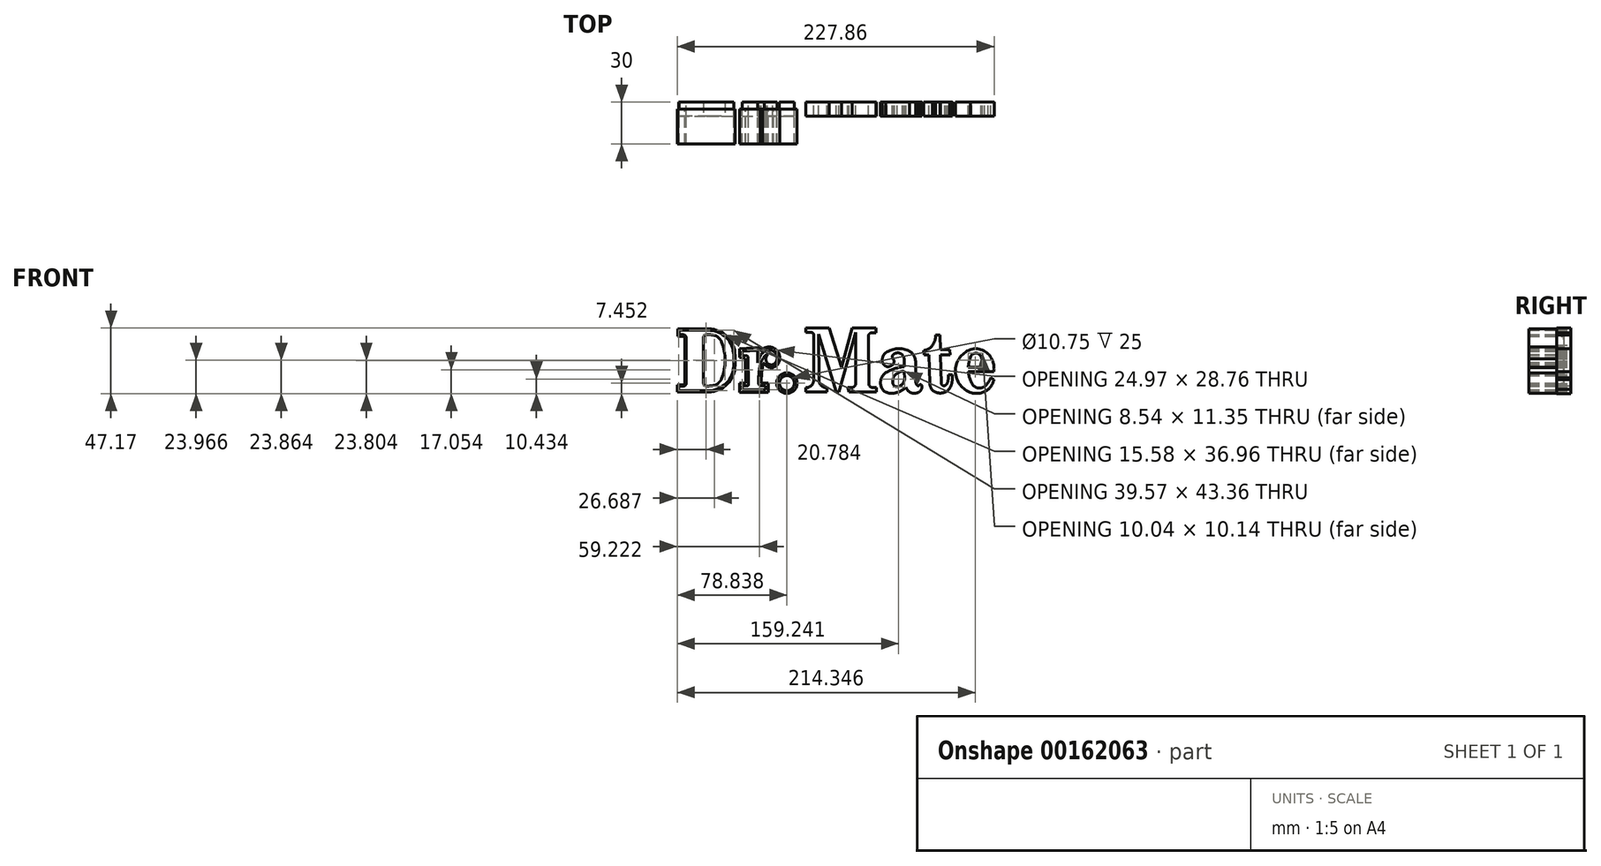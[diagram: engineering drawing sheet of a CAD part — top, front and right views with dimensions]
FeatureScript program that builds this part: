
annotation { "Feature Type Name" : "Feature", "Feature Type Description" : "" }
export const myFeature = defineFeature(function(context is Context, id is Id, definition is map)
    precondition{}
    {
        {
            var Q0;
            Q0=qCreatedBy(makeId("Front.planeOp"),FACE);
            var sketch = newSketch(context, id + "F0", { "sketchPlane" : qUnion([Q0])});
            skLineSegment(sketch, "E0", {"start": v(23.83, 45.48) * mm, "end": v(2.7, 45.48) * mm});
            skLineSegment(sketch, "E1", {"start": v(2.7, 45.48) * mm, "end": v(2.7, 42.24) * mm});
            skLineSegment(sketch, "E2", {"start": v(2.7, 42.24) * mm, "end": v(5.73, 42.24) * mm});
            skLineSegment(sketch, "E3", {"start": v(7.73, 40.24) * mm, "end": v(7.73, 7.24) * mm});
            skLineSegment(sketch, "E4", {"start": v(5.73, 5.24) * mm, "end": v(2.36, 5.24) * mm});
            skLineSegment(sketch, "E5", {"start": v(2.36, 5.24) * mm, "end": v(2.36, 2.11) * mm});
            skLineSegment(sketch, "E6", {"start": v(2.36, 2.11) * mm, "end": v(23.83, 2.11) * mm});
            skPoint(sketch, "E7.visualSharp", {"position": v(7.73, 42.24) * mm});
            skArc(sketch, "E7.filletArc", {"start": v(7.73, 40.24) * mm, "mid": v(7.14, 41.66) * mm, "end": v(5.73, 42.24) * mm});
            skPoint(sketch, "E8.visualSharp", {"position": v(7.73, 5.24) * mm});
            skArc(sketch, "E8.filletArc", {"start": v(5.73, 5.24) * mm, "mid": v(7.14, 5.83) * mm, "end": v(7.73, 7.24) * mm});
            skLineSegment(sketch, "E9", {"start": v(41.93, 27.38) * mm, "end": v(41.93, 20.21) * mm});
            skPoint(sketch, "E10.visualSharp", {"position": v(41.93, 45.48) * mm});
            skArc(sketch, "E10.filletArc", {"start": v(41.93, 27.38) * mm, "mid": v(36.63, 40.17) * mm, "end": v(23.83, 45.48) * mm});
            skPoint(sketch, "E11.visualSharp", {"position": v(41.93, 2.11) * mm});
            skArc(sketch, "E11.filletArc", {"start": v(23.83, 2.11) * mm, "mid": v(36.63, 7.41) * mm, "end": v(41.93, 20.21) * mm});
            skSolve(sketch);
        }
        {
            var Q0;
            Q0 = qSketchRegion(id + "F0", true);
            extrude(context, id + "F1", {"entities" : qUnion([Q0]), "endBound" : BoundingType.SYMMETRIC, "depth" : 10 * mm});
        }
        {
            var Q0;
            Q0=qCreatedBy(makeId("Front.planeOp"),FACE);
            var sketch = newSketch(context, id + "F2", { "sketchPlane" : qUnion([Q0])});
            skLineSegment(sketch, "E12", {"start": v(20.26, 40.33) * mm, "end": v(20.26, 7.37) * mm});
            skLineSegment(sketch, "E13", {"start": v(22.26, 5.37) * mm, "end": v(23.68, 5.37) * mm});
            skLineSegment(sketch, "E14", {"start": v(22.26, 42.33) * mm, "end": v(23.68, 42.33) * mm});
            skPoint(sketch, "E15.visualSharp", {"position": v(20.26, 42.33) * mm});
            skArc(sketch, "E15.filletArc", {"start": v(22.26, 42.33) * mm, "mid": v(20.84, 41.75) * mm, "end": v(20.26, 40.33) * mm});
            skPoint(sketch, "E16.visualSharp", {"position": v(20.26, 5.37) * mm});
            skArc(sketch, "E16.filletArc", {"start": v(20.26, 7.37) * mm, "mid": v(20.84, 5.96) * mm, "end": v(22.26, 5.37) * mm});
            skPoint(sketch, "E17.visualSharp", {"position": v(41.68, 42.33) * mm});
            skArc(sketch, "E17.filletArc", {"start": v(29.92, 41.22) * mm, "mid": v(26.85, 42.05) * mm, "end": v(23.68, 42.33) * mm});
            skPoint(sketch, "E18.visualSharp", {"position": v(41.68, 5.37) * mm});
            skArc(sketch, "E18.filletArc", {"start": v(23.68, 5.37) * mm, "mid": v(26.85, 5.66) * mm, "end": v(29.92, 6.49) * mm});
            skArc(sketch, "E19", {"start": v(29.92, 6.49) * mm, "mid": v(31.56, 8.17) * mm, "end": v(33.02, 10) * mm});
            skArc(sketch, "E20.trimOffspring", {"start": v(33.02, 37.7) * mm, "mid": v(31.56, 39.54) * mm, "end": v(29.92, 41.22) * mm});
            skArc(sketch, "E21", {"start": v(33.02, 10) * mm, "mid": v(35.84, 23.85) * mm, "end": v(33.02, 37.7) * mm});
            skSolve(sketch);
        }
        {
            var Q0;
            Q0 = qSketchRegion(id + "F2", true);
            extrude(context, id + "F3", {"entities" : qUnion([Q0]), "operationType" : NewBodyOperationType.REMOVE, "endBound" : BoundingType.SYMMETRIC, "oppositeDirection" : true, "depth" : 25 * mm});
        }
        {
            var Q0;
            Q0=makeQuery(id+"F3.boolean.opBoolean","COPY",EDGE,{"derivedFrom":makeQuery(id+"F3.opExtrude","SWEPT_EDGE",EDGE,{"disambiguationData":[OSD([sQuery(id+"F2.wireOp",EDGE,"E19"),sQuery(id+"F2.wireOp",EDGE,"E21")])]})});
            var Q1;
            Q1=makeQuery(id+"F3.boolean.opBoolean","COPY",EDGE,{"derivedFrom":makeQuery(id+"F3.opExtrude","SWEPT_EDGE",EDGE,{"disambiguationData":[OSD([sQuery(id+"F2.wireOp",EDGE,"E18.filletArc"),sQuery(id+"F2.wireOp",EDGE,"E19")])]})});
            var Q2;
            Q2=makeQuery(id+"F3.boolean.opBoolean","COPY",EDGE,{"derivedFrom":makeQuery(id+"F3.opExtrude","SWEPT_EDGE",EDGE,{"disambiguationData":[OSD([sQuery(id+"F2.wireOp",EDGE,"E20.trimOffspring"),sQuery(id+"F2.wireOp",EDGE,"E21")])]})});
            var Q3;
            Q3=makeQuery(id+"F3.boolean.opBoolean","COPY",EDGE,{"derivedFrom":makeQuery(id+"F3.opExtrude","SWEPT_EDGE",EDGE,{"disambiguationData":[OSD([sQuery(id+"F2.wireOp",EDGE,"E17.filletArc"),sQuery(id+"F2.wireOp",EDGE,"E20.trimOffspring")])]})});
            fillet(context, id + "F4", {"entities" : qUnion([Q0, Q1, Q2, Q3]), "radius" : 5 * mm, "tangentPropagation" : true, "allowEdgeOverflow" : false});
        }
        {
            var Q0;
            Q0=qCreatedBy(makeId("Front.planeOp"),FACE);
            var sketch = newSketch(context, id + "F5", { "sketchPlane" : qUnion([Q0])});
            skLineSegment(sketch, "E22", {"start": v(48.1, 30.42) * mm, "end": v(48.1, 27.61) * mm});
            skLineSegment(sketch, "E23", {"start": v(48.1, 30.42) * mm, "end": v(59.09, 30.93) * mm});
            skLineSegment(sketch, "E24", {"start": v(48.1, 2.66) * mm, "end": v(64.8, 2.66) * mm});
            skLineSegment(sketch, "E25", {"start": v(59.09, 30.93) * mm, "end": v(59.09, 22.2) * mm});
            skLineSegment(sketch, "E26", {"start": v(48.1, 5.47) * mm, "end": v(51.51, 5.47) * mm});
            skLineSegment(sketch, "E27", {"start": v(48.1, 27.61) * mm, "end": v(51.46, 27.04) * mm});
            skLineSegment(sketch, "E28", {"start": v(64.8, 5.47) * mm, "end": v(64.8, 2.66) * mm});
            skLineSegment(sketch, "E29.trimOffspring", {"start": v(52.29, 26.06) * mm, "end": v(52.51, 6.48) * mm});
            skLineSegment(sketch, "E30.trimOffspring", {"start": v(61.83, 5.47) * mm, "end": v(64.8, 5.47) * mm});
            skLineSegment(sketch, "E31.trimOffspring", {"start": v(48.1, 5.47) * mm, "end": v(48.1, 2.66) * mm});
            skArc(sketch, "E32", {"start": v(73.07, 24.94) * mm, "mid": v(70.3, 30.62) * mm, "end": v(64, 30.34) * mm});
            skArc(sketch, "E33", {"start": v(69.92, 20.7) * mm, "mid": v(72.14, 22.34) * mm, "end": v(73.07, 24.94) * mm});
            skArc(sketch, "E34", {"start": v(64, 30.34) * mm, "mid": v(60.9, 26.65) * mm, "end": v(59.09, 22.2) * mm});
            skArc(sketch, "E35", {"start": v(65.86, 22.25) * mm, "mid": v(67.65, 20.85) * mm, "end": v(69.92, 20.7) * mm});
            skArc(sketch, "E36", {"start": v(66.1, 27.52) * mm, "mid": v(65.06, 24.93) * mm, "end": v(65.86, 22.25) * mm});
            skArc(sketch, "E37", {"start": v(59.89, 6.98) * mm, "mid": v(60.62, 5.92) * mm, "end": v(61.83, 5.47) * mm});
            skArc(sketch, "E38", {"start": v(60.03, 13.08) * mm, "mid": v(59.8, 10.03) * mm, "end": v(59.89, 6.98) * mm});
            skArc(sketch, "E39", {"start": v(60.96, 20.37) * mm, "mid": v(60.34, 16.75) * mm, "end": v(60.03, 13.08) * mm});
            skArc(sketch, "E40", {"start": v(65.5, 27.94) * mm, "mid": v(62.63, 24.52) * mm, "end": v(60.96, 20.37) * mm});
            skArc(sketch, "E41", {"start": v(66.1, 27.52) * mm, "mid": v(65.98, 27.98) * mm, "end": v(65.5, 27.94) * mm});
            skPoint(sketch, "E42.visualSharp", {"position": v(52.28, 26.9) * mm});
            skArc(sketch, "E42.filletArc", {"start": v(52.29, 26.06) * mm, "mid": v(52.05, 26.7) * mm, "end": v(51.46, 27.04) * mm});
            skPoint(sketch, "E43.visualSharp", {"position": v(52.52, 5.47) * mm});
            skArc(sketch, "E43.filletArc", {"start": v(51.51, 5.47) * mm, "mid": v(52.22, 5.77) * mm, "end": v(52.51, 6.48) * mm});
            skSolve(sketch);
        }
        {
            var Q0;
            Q0 = qSketchRegion(id + "F5", true);
            extrude(context, id + "F6", {"entities" : qUnion([Q0]), "endBound" : BoundingType.SYMMETRIC, "depth" : 10 * mm});
        }
        {
            var Q0;
            Q0=qCreatedBy(makeId("Front.planeOp"),FACE);
            var sketch = newSketch(context, id + "F7", { "sketchPlane" : qUnion([Q0])});
            skCircle(sketch, "E44", {"center": v(80.2, 7.44) * mm, "radius": 5.38 * mm});
            skSolve(sketch);
        }
        {
            var Q0;
            Q0 = qSketchRegion(id + "F7", true);
            extrude(context, id + "F8", {"entities" : qUnion([Q0]), "endBound" : BoundingType.SYMMETRIC, "depth" : 10 * mm});
        }
        {
            var Q0;
            Q0=qCreatedBy(makeId("Front.planeOp"),FACE);
            var sketch = newSketch(context, id + "F9", { "sketchPlane" : qUnion([Q0])});
            skLineSegment(sketch, "E45", {"start": v(93.8, 47.16) * mm, "end": v(110.75, 47.16) * mm});
            skLineSegment(sketch, "E46", {"start": v(127.22, 47.16) * mm, "end": v(119.38, 19.02) * mm});
            skLineSegment(sketch, "E47", {"start": v(93.8, 47.16) * mm, "end": v(93.8, 43.88) * mm});
            skLineSegment(sketch, "E48", {"start": v(99.4, 42.37) * mm, "end": v(99.4, 9.27) * mm});
            skLineSegment(sketch, "E49", {"start": v(93.8, 1.02) * mm, "end": v(108.94, 1.02) * mm});
            skLineSegment(sketch, "E50", {"start": v(102.92, 42.74) * mm, "end": v(103.28, 9.22) * mm});
            skLineSegment(sketch, "E51", {"start": v(102.92, 42.74) * mm, "end": v(115.57, 1.02) * mm});
            skLineSegment(sketch, "E52", {"start": v(110.75, 47.16) * mm, "end": v(119.38, 19.02) * mm});
            skLineSegment(sketch, "E53", {"start": v(129.69, 43.89) * mm, "end": v(129.69, 7.07) * mm});
            skLineSegment(sketch, "E54", {"start": v(138.75, 40.98) * mm, "end": v(139.12, 7.04) * mm});
            skLineSegment(sketch, "E55", {"start": v(144.36, 47.16) * mm, "end": v(144.39, 43.8) * mm});
            skLineSegment(sketch, "E56", {"start": v(93.8, 43.88) * mm, "end": v(97.9, 43.87) * mm});
            skLineSegment(sketch, "E57.0", {"start": v(93.8, 4.27) * mm, "end": v(94.4, 4.27) * mm});
            skPoint(sketch, "E58.orphan", {"position": v(90.95, 43.89) * mm});
            skPoint(sketch, "E59.orphan", {"position": v(90.95, 47.16) * mm});
            skLineSegment(sketch, "E60.trimOffspring", {"start": v(144.68, 4.27) * mm, "end": v(144.7, 1.02) * mm});
            skLineSegment(sketch, "E61.trimOffspring", {"start": v(141.56, 43.8) * mm, "end": v(144.39, 43.8) * mm});
            skLineSegment(sketch, "E62.trimOffspring", {"start": v(127.22, 47.16) * mm, "end": v(144.36, 47.16) * mm});
            skLineSegment(sketch, "E63.trimOffspring", {"start": v(93.8, 4.27) * mm, "end": v(93.8, 1.02) * mm});
            skLineSegment(sketch, "E64.trimOffspring", {"start": v(117.74, 1.02) * mm, "end": v(129.69, 43.89) * mm});
            skLineSegment(sketch, "E65.trimOffspring", {"start": v(123.9, 4.27) * mm, "end": v(124.9, 1.02) * mm});
            skLineSegment(sketch, "E66.trimOffspring", {"start": v(108.28, 4.27) * mm, "end": v(108.96, 4.27) * mm});
            skLineSegment(sketch, "E67.trimOffspring", {"start": v(123.9, 4.27) * mm, "end": v(126.89, 4.27) * mm});
            skLineSegment(sketch, "E68.trimOffspring", {"start": v(124.9, 1.02) * mm, "end": v(144.7, 1.02) * mm});
            skLineSegment(sketch, "E69.trimOffspring", {"start": v(141.92, 4.27) * mm, "end": v(144.68, 4.27) * mm});
            skPoint(sketch, "E70.startSnap0", {"position": v(108.96, 4.27) * mm});
            skLineSegment(sketch, "E71", {"start": v(108.94, 4.27) * mm, "end": v(108.94, 1.02) * mm});
            skLineSegment(sketch, "E72.trimOffspring", {"start": v(115.57, 1.02) * mm, "end": v(117.74, 1.02) * mm});
            skPoint(sketch, "E73.visualSharp", {"position": v(99.4, 43.87) * mm});
            skArc(sketch, "E73.filletArc", {"start": v(99.4, 42.37) * mm, "mid": v(98.96, 43.43) * mm, "end": v(97.9, 43.87) * mm});
            skPoint(sketch, "E74.visualSharp", {"position": v(99.4, 4.27) * mm});
            skArc(sketch, "E74.filletArc", {"start": v(94.4, 4.27) * mm, "mid": v(97.94, 5.74) * mm, "end": v(99.4, 9.27) * mm});
            skPoint(sketch, "E75.visualSharp", {"position": v(103.34, 4.27) * mm});
            skArc(sketch, "E75.filletArc", {"start": v(103.28, 9.22) * mm, "mid": v(104.77, 5.72) * mm, "end": v(108.28, 4.27) * mm});
            skPoint(sketch, "E76.visualSharp", {"position": v(129.69, 4.27) * mm});
            skArc(sketch, "E76.filletArc", {"start": v(126.89, 4.27) * mm, "mid": v(128.87, 5.1) * mm, "end": v(129.69, 7.07) * mm});
            skPoint(sketch, "E77.visualSharp", {"position": v(139.15, 4.27) * mm});
            skArc(sketch, "E77.filletArc", {"start": v(139.12, 7.04) * mm, "mid": v(139.95, 5.08) * mm, "end": v(141.92, 4.27) * mm});
            skPoint(sketch, "E78.visualSharp", {"position": v(138.72, 43.81) * mm});
            skArc(sketch, "E78.filletArc", {"start": v(141.56, 43.8) * mm, "mid": v(139.56, 42.98) * mm, "end": v(138.75, 40.98) * mm});
            skSolve(sketch);
        }
        {
            var Q0;
            Q0 = qSketchRegion(id + "F9", true);
            extrude(context, id + "F10", {"entities" : qUnion([Q0]), "endBound" : BoundingType.SYMMETRIC, "depth" : 10 * mm});
        }
        {
            var Q0;
            Q0=qCreatedBy(makeId("Front.planeOp"),FACE);
            var sketch = newSketch(context, id + "F11", { "sketchPlane" : qUnion([Q0])});
            skArc(sketch, "E79", {"start": v(172.7, 22.65) * mm, "mid": v(171.66, 27.12) * mm, "end": v(168.48, 30.43) * mm});
            skLineSegment(sketch, "E80", {"start": v(172.7, 22.65) * mm, "end": v(172.93, 8.42) * mm});
            skArc(sketch, "E81", {"start": v(168.48, 30.43) * mm, "mid": v(159.76, 32.2) * mm, "end": v(151.36, 29.26) * mm});
            skArc(sketch, "E82", {"start": v(151.36, 29.26) * mm, "mid": v(149.3, 26.59) * mm, "end": v(148.75, 23.26) * mm});
            skArc(sketch, "E83", {"start": v(148.75, 23.26) * mm, "mid": v(149.95, 20.7) * mm, "end": v(152.36, 19.26) * mm});
            skArc(sketch, "E84", {"start": v(152.36, 19.26) * mm, "mid": v(155.23, 19.9) * mm, "end": v(157.14, 22.15) * mm});
            skArc(sketch, "E85", {"start": v(157.14, 22.15) * mm, "mid": v(157.07, 24.2) * mm, "end": v(155.97, 25.93) * mm});
            skArc(sketch, "E86", {"start": v(156.97, 28.2) * mm, "mid": v(156.13, 27.22) * mm, "end": v(155.97, 25.93) * mm});
            skArc(sketch, "E87", {"start": v(164.45, 25.33) * mm, "mid": v(161.55, 28.93) * mm, "end": v(156.97, 28.2) * mm});
            skLineSegment(sketch, "E88", {"start": v(164.45, 25.33) * mm, "end": v(164.87, 11.05) * mm});
            skArc(sketch, "E89", {"start": v(164.74, 15.46) * mm, "mid": v(164.18, 15.94) * mm, "end": v(163.46, 16.1) * mm});
            skArc(sketch, "E90", {"start": v(164.63, 19.28) * mm, "mid": v(157.74, 17.88) * mm, "end": v(151.36, 14.93) * mm});
            skArc(sketch, "E91", {"start": v(151.36, 14.93) * mm, "mid": v(147.6, 8.68) * mm, "end": v(150.1, 1.82) * mm});
            skArc(sketch, "E92", {"start": v(150.1, 1.82) * mm, "mid": v(153.65, 0.29) * mm, "end": v(157.51, 0.28) * mm});
            skArc(sketch, "E93", {"start": v(157.51, 0.28) * mm, "mid": v(162.02, 1.68) * mm, "end": v(165.85, 4.44) * mm});
            skArc(sketch, "E94", {"start": v(159.52, 4.75) * mm, "mid": v(163.4, 6.87) * mm, "end": v(164.87, 11.05) * mm});
            skArc(sketch, "E95", {"start": v(156.5, 7.23) * mm, "mid": v(157.54, 5.41) * mm, "end": v(159.52, 4.75) * mm});
            skArc(sketch, "E96", {"start": v(157.54, 12.92) * mm, "mid": v(156.46, 10.18) * mm, "end": v(156.5, 7.23) * mm});
            skPoint(sketch, "E96.startSnap0", {"position": v(157.54, 5.41) * mm});
            skArc(sketch, "E97", {"start": v(163.46, 16.1) * mm, "mid": v(160.31, 14.86) * mm, "end": v(157.54, 12.92) * mm});
            skArc(sketch, "E98", {"start": v(172.93, 8.42) * mm, "mid": v(173.22, 7) * mm, "end": v(174.02, 5.8) * mm});
            skArc(sketch, "E99", {"start": v(174.02, 5.8) * mm, "mid": v(174.98, 5.66) * mm, "end": v(175.7, 6.3) * mm});
            skArc(sketch, "E100", {"start": v(177.42, 5.6) * mm, "mid": v(176.71, 6.32) * mm, "end": v(175.7, 6.3) * mm});
            skArc(sketch, "E101", {"start": v(174.62, 0.74) * mm, "mid": v(176.77, 2.73) * mm, "end": v(177.42, 5.6) * mm});
            skArc(sketch, "E102", {"start": v(165.85, 4.44) * mm, "mid": v(167.1, 2.35) * mm, "end": v(168.94, 0.77) * mm});
            skArc(sketch, "E103", {"start": v(168.94, 0.77) * mm, "mid": v(171.78, 0.05) * mm, "end": v(174.62, 0.74) * mm});
            skSolve(sketch);
        }
        {
            var Q0;
            Q0 = qSketchRegion(id + "F11", true);
            extrude(context, id + "F12", {"entities" : qUnion([Q0]), "endBound" : BoundingType.SYMMETRIC, "depth" : 10 * mm});
        }
        {
            var Q0;
            Q0=qCreatedBy(makeId("Front.planeOp"),FACE);
            var sketch = newSketch(context, id + "F13", { "sketchPlane" : qUnion([Q0])});
            skLineSegment(sketch, "E104", {"start": v(187.18, 42.16) * mm, "end": v(190.44, 42.1) * mm});
            skLineSegment(sketch, "E105", {"start": v(190.44, 42.1) * mm, "end": v(190.67, 31.73) * mm});
            skLineSegment(sketch, "E106", {"start": v(178.8, 27.63) * mm, "end": v(182.53, 27.63) * mm});
            skLineSegment(sketch, "E107", {"start": v(197.44, 31.73) * mm, "end": v(190.67, 31.73) * mm});
            skLineSegment(sketch, "E108", {"start": v(178.7, 31.04) * mm, "end": v(178.8, 27.63) * mm});
            skLineSegment(sketch, "E109", {"start": v(197.44, 31.73) * mm, "end": v(197.59, 27.63) * mm});
            skLineSegment(sketch, "E110", {"start": v(196.3, 13.37) * mm, "end": v(199.27, 13.37) * mm});
            skArc(sketch, "E111", {"start": v(182.9, 7.56) * mm, "mid": v(183.7, 4.23) * mm, "end": v(185.78, 1.52) * mm});
            skArc(sketch, "E112", {"start": v(185.78, 1.52) * mm, "mid": v(189.97, 0.3) * mm, "end": v(194.28, 0.99) * mm});
            skArc(sketch, "E113", {"start": v(194.28, 0.99) * mm, "mid": v(196.72, 3.04) * mm, "end": v(198.37, 5.77) * mm});
            skArc(sketch, "E114", {"start": v(198.37, 5.77) * mm, "mid": v(199.19, 9.53) * mm, "end": v(199.27, 13.37) * mm});
            skArc(sketch, "E115", {"start": v(191.2, 7.87) * mm, "mid": v(191.86, 6.09) * mm, "end": v(193.7, 5.6) * mm});
            skArc(sketch, "E116", {"start": v(193.7, 5.6) * mm, "mid": v(194.65, 6.17) * mm, "end": v(195.36, 7.01) * mm});
            skArc(sketch, "E117", {"start": v(195.36, 7.01) * mm, "mid": v(196.26, 10.12) * mm, "end": v(196.3, 13.37) * mm});
            skLineSegment(sketch, "E118.trimOffspring", {"start": v(190.76, 27.63) * mm, "end": v(197.59, 27.63) * mm});
            skLineSegment(sketch, "E119.trimOffspring", {"start": v(182.53, 27.63) * mm, "end": v(182.9, 7.56) * mm});
            skLineSegment(sketch, "E120.trimOffspring", {"start": v(190.76, 27.63) * mm, "end": v(191.22, 7.26) * mm});
            skPoint(sketch, "E121.visualSharp", {"position": v(182.26, 42.25) * mm});
            skArc(sketch, "E122", {"start": v(178.7, 31.04) * mm, "mid": v(182.27, 32.15) * mm, "end": v(185, 34.71) * mm});
            skArc(sketch, "E123", {"start": v(185, 34.71) * mm, "mid": v(186.7, 38.26) * mm, "end": v(187.18, 42.16) * mm});
            skSolve(sketch);
        }
        {
            var Q0;
            Q0 = qSketchRegion(id + "F13", true);
            extrude(context, id + "F14", {"entities" : qUnion([Q0]), "endBound" : BoundingType.SYMMETRIC, "depth" : 10 * mm});
        }
        {
            var Q0;
            Q0=qCreatedBy(makeId("Front.planeOp"),FACE);
            var sketch = newSketch(context, id + "F15", { "sketchPlane" : qUnion([Q0])});
            skLineSegment(sketch, "E124", {"start": v(210.69, 18.89) * mm, "end": v(220.1, 18.89) * mm});
            skLineSegment(sketch, "E125", {"start": v(210.74, 15.7) * mm, "end": v(229.12, 15.7) * mm});
            skLineSegment(sketch, "E126", {"start": v(226.7, 11.4) * mm, "end": v(229.2, 10.1) * mm});
            skArc(sketch, "E127", {"start": v(212.17, 31.58) * mm, "mid": v(201.46, 15.7) * mm, "end": v(213.05, 0.47) * mm});
            skArc(sketch, "E128", {"start": v(228.31, 23.2) * mm, "mid": v(221.93, 30.65) * mm, "end": v(212.17, 31.58) * mm});
            skArc(sketch, "E129.trimOffspring", {"start": v(229.12, 15.7) * mm, "mid": v(229.12, 19.5) * mm, "end": v(228.31, 23.2) * mm});
            skArc(sketch, "E130", {"start": v(219.75, 26.59) * mm, "mid": v(216.18, 29.03) * mm, "end": v(212.55, 26.67) * mm});
            skArc(sketch, "E131", {"start": v(220.58, 20.03) * mm, "mid": v(220.63, 23.37) * mm, "end": v(219.75, 26.59) * mm});
            skArc(sketch, "E132", {"start": v(220.1, 18.89) * mm, "mid": v(220.37, 19.45) * mm, "end": v(220.58, 20.03) * mm});
            skArc(sketch, "E133", {"start": v(213.05, 0.47) * mm, "mid": v(219.37, 0.28) * mm, "end": v(225.06, 3.02) * mm});
            skArc(sketch, "E134", {"start": v(225.06, 3.02) * mm, "mid": v(227.65, 6.26) * mm, "end": v(229.2, 10.1) * mm});
            skArc(sketch, "E135", {"start": v(213.34, 7.06) * mm, "mid": v(217.36, 4.02) * mm, "end": v(222.3, 5.01) * mm});
            skArc(sketch, "E136", {"start": v(222.3, 5.01) * mm, "mid": v(225.03, 7.85) * mm, "end": v(226.7, 11.4) * mm});
            skArc(sketch, "E137", {"start": v(212.55, 26.67) * mm, "mid": v(211.27, 22.86) * mm, "end": v(210.69, 18.89) * mm});
            skArc(sketch, "E138.trimOffspring", {"start": v(210.74, 15.7) * mm, "mid": v(211.6, 11.25) * mm, "end": v(213.34, 7.06) * mm});
            skSolve(sketch);
        }
        {
            var Q0;
            Q0 = qSketchRegion(id + "F15", true);
            extrude(context, id + "F16", {"entities" : qUnion([Q0]), "endBound" : BoundingType.SYMMETRIC, "depth" : 10 * mm});
        }
        {
            var Q0;
            Q0=qCreatedBy(makeId("Front.planeOp"),FACE);
            var sketch = newSketch(context, id + "F17", { "sketchPlane" : qUnion([Q0])});
            skLineSegment(sketch, "E139.0", {"start": v(22.26, 42.33) * mm, "end": v(23.68, 42.33) * mm});
            skArc(sketch, "E139.1", {"start": v(28.62, 41.64) * mm, "mid": v(29.82, 41.12) * mm, "end": v(30.85, 40.3) * mm});
            skArc(sketch, "E139.2", {"start": v(30.85, 7.4) * mm, "mid": v(29.82, 6.59) * mm, "end": v(28.62, 6.07) * mm});
            skArc(sketch, "E139.3", {"start": v(5.73, 5.24) * mm, "mid": v(7.14, 5.83) * mm, "end": v(7.73, 7.24) * mm});
            skArc(sketch, "E139.4", {"start": v(41.93, 27.38) * mm, "mid": v(36.63, 40.17) * mm, "end": v(23.83, 45.48) * mm});
            skArc(sketch, "E139.5", {"start": v(23.83, 2.11) * mm, "mid": v(36.63, 7.41) * mm, "end": v(41.93, 20.21) * mm});
            skArc(sketch, "E139.6", {"start": v(22.26, 42.33) * mm, "mid": v(20.84, 41.75) * mm, "end": v(20.26, 40.33) * mm});
            skArc(sketch, "E139.7", {"start": v(28.62, 41.64) * mm, "mid": v(26.18, 42.16) * mm, "end": v(23.68, 42.33) * mm});
            skArc(sketch, "E139.8", {"start": v(30.85, 7.4) * mm, "mid": v(31.76, 8.4) * mm, "end": v(32.6, 9.45) * mm});
            skArc(sketch, "E139.9", {"start": v(32.6, 38.26) * mm, "mid": v(31.76, 39.3) * mm, "end": v(30.85, 40.3) * mm});
            skArc(sketch, "E139.10", {"start": v(33.28, 10.63) * mm, "mid": v(35.84, 23.85) * mm, "end": v(33.28, 37.08) * mm});
            skArc(sketch, "E139.11", {"start": v(23.68, 5.37) * mm, "mid": v(26.18, 5.55) * mm, "end": v(28.62, 6.07) * mm});
            skLineSegment(sketch, "E139.12", {"start": v(23.83, 45.48) * mm, "end": v(2.7, 45.48) * mm});
            skLineSegment(sketch, "E139.13", {"start": v(2.7, 45.48) * mm, "end": v(2.7, 42.24) * mm});
            skLineSegment(sketch, "E139.16", {"start": v(22.26, 5.37) * mm, "end": v(23.68, 5.37) * mm});
            skLineSegment(sketch, "E139.20", {"start": v(20.26, 40.33) * mm, "end": v(20.26, 7.37) * mm});
            skArc(sketch, "E139.22", {"start": v(32.6, 38.26) * mm, "mid": v(32.98, 37.7) * mm, "end": v(33.28, 37.08) * mm});
            skArc(sketch, "E139.25", {"start": v(30.85, 40.3) * mm, "mid": v(29.82, 41.12) * mm, "end": v(28.62, 41.64) * mm});
            skArc(sketch, "E139.28", {"start": v(33.28, 10.63) * mm, "mid": v(32.98, 10.01) * mm, "end": v(32.6, 9.45) * mm});
            skLineSegment(sketch, "E139.29", {"start": v(41.93, 27.38) * mm, "end": v(41.93, 20.21) * mm});
            skArc(sketch, "E139.30", {"start": v(41.93, 27.38) * mm, "mid": v(36.63, 40.17) * mm, "end": v(23.83, 45.48) * mm});
            skLineSegment(sketch, "E139.31", {"start": v(2.7, 42.24) * mm, "end": v(5.73, 42.24) * mm});
            skArc(sketch, "E139.32", {"start": v(23.83, 2.11) * mm, "mid": v(36.63, 7.41) * mm, "end": v(41.93, 20.21) * mm});
            skLineSegment(sketch, "E139.33", {"start": v(7.73, 40.24) * mm, "end": v(7.73, 7.24) * mm});
            skLineSegment(sketch, "E139.34", {"start": v(5.73, 5.24) * mm, "end": v(2.36, 5.24) * mm});
            skLineSegment(sketch, "E139.35", {"start": v(2.36, 5.24) * mm, "end": v(2.36, 2.11) * mm});
            skLineSegment(sketch, "E139.36", {"start": v(2.36, 2.11) * mm, "end": v(23.83, 2.11) * mm});
            skArc(sketch, "E139.37", {"start": v(7.73, 40.24) * mm, "mid": v(7.14, 41.66) * mm, "end": v(5.73, 42.24) * mm});
            skArc(sketch, "E139.38", {"start": v(22.26, 42.33) * mm, "mid": v(20.84, 41.75) * mm, "end": v(20.26, 40.33) * mm});
            skArc(sketch, "E139.39", {"start": v(20.26, 7.37) * mm, "mid": v(20.84, 5.96) * mm, "end": v(22.26, 5.37) * mm});
            skArc(sketch, "E139.40", {"start": v(32.6, 38.26) * mm, "mid": v(31.76, 39.3) * mm, "end": v(30.85, 40.3) * mm});
            skArc(sketch, "E139.41", {"start": v(33.28, 10.63) * mm, "mid": v(35.84, 23.85) * mm, "end": v(33.28, 37.08) * mm});
            skLineSegment(sketch, "E139.42", {"start": v(2.7, 45.48) * mm, "end": v(2.7, 42.24) * mm});
            skLineSegment(sketch, "E139.53", {"start": v(23.83, 45.48) * mm, "end": v(2.7, 45.48) * mm});
            skLineSegment(sketch, "E139.54", {"start": v(22.26, 42.33) * mm, "end": v(23.68, 42.33) * mm});
            skLineSegment(sketch, "E139.58", {"start": v(20.26, 40.33) * mm, "end": v(20.26, 7.37) * mm});
            skLineSegment(sketch, "E139.59", {"start": v(22.26, 5.37) * mm, "end": v(23.68, 5.37) * mm});
            skArc(sketch, "E139.60", {"start": v(28.62, 6.07) * mm, "mid": v(29.82, 6.59) * mm, "end": v(30.85, 7.4) * mm});
            skLineSegment(sketch, "E139.64", {"start": v(41.93, 27.38) * mm, "end": v(41.93, 20.21) * mm});
            skLineSegment(sketch, "E139.65", {"start": v(2.7, 42.24) * mm, "end": v(5.73, 42.24) * mm});
            skLineSegment(sketch, "E139.66", {"start": v(7.73, 40.24) * mm, "end": v(7.73, 7.24) * mm});
            skLineSegment(sketch, "E139.67", {"start": v(5.73, 5.24) * mm, "end": v(2.36, 5.24) * mm});
            skLineSegment(sketch, "E139.68", {"start": v(2.36, 5.24) * mm, "end": v(2.36, 2.11) * mm});
            skLineSegment(sketch, "E139.69", {"start": v(2.36, 2.11) * mm, "end": v(23.83, 2.11) * mm});
            skArc(sketch, "E139.70", {"start": v(5.73, 5.24) * mm, "mid": v(7.14, 5.83) * mm, "end": v(7.73, 7.24) * mm});
            skArc(sketch, "E139.71", {"start": v(20.26, 7.37) * mm, "mid": v(20.84, 5.96) * mm, "end": v(22.26, 5.37) * mm});
            skArc(sketch, "E139.72", {"start": v(28.62, 41.64) * mm, "mid": v(26.18, 42.16) * mm, "end": v(23.68, 42.33) * mm});
            skArc(sketch, "E139.73", {"start": v(30.85, 7.4) * mm, "mid": v(31.76, 8.4) * mm, "end": v(32.6, 9.45) * mm});
            skArc(sketch, "E139.74", {"start": v(23.68, 5.37) * mm, "mid": v(26.18, 5.55) * mm, "end": v(28.62, 6.07) * mm});
            skArc(sketch, "E139.75", {"start": v(33.28, 37.08) * mm, "mid": v(32.98, 37.7) * mm, "end": v(32.6, 38.26) * mm});
            skArc(sketch, "E139.76", {"start": v(32.6, 9.45) * mm, "mid": v(32.98, 10.01) * mm, "end": v(33.28, 10.63) * mm});
            skArc(sketch, "E139.77", {"start": v(7.73, 40.24) * mm, "mid": v(7.14, 41.66) * mm, "end": v(5.73, 42.24) * mm});
            skLineSegment(sketch, "E140.0", {"start": v(22.26, 40.33) * mm, "end": v(22.26, 7.37) * mm});
            skLineSegment(sketch, "E141.0", {"start": v(22.26, 7.37) * mm, "end": v(23.68, 7.37) * mm});
            skArc(sketch, "E141.1", {"start": v(23.68, 7.37) * mm, "mid": v(26.3, 7.6) * mm, "end": v(28.85, 8.23) * mm});
            skArc(sketch, "E141.2", {"start": v(28.85, 8.23) * mm, "mid": v(30.12, 9.56) * mm, "end": v(31.27, 11) * mm});
            skLineSegment(sketch, "E141.3", {"start": v(22.26, 40.33) * mm, "end": v(23.68, 40.33) * mm});
            skArc(sketch, "E141.4", {"start": v(28.85, 39.47) * mm, "mid": v(26.3, 40.12) * mm, "end": v(23.68, 40.33) * mm});
            skArc(sketch, "E141.5", {"start": v(31.27, 36.71) * mm, "mid": v(30.12, 38.14) * mm, "end": v(28.85, 39.47) * mm});
            skArc(sketch, "E141.6", {"start": v(31.27, 11) * mm, "mid": v(33.84, 23.85) * mm, "end": v(31.27, 36.71) * mm});
            skLineSegment(sketch, "E142.0", {"start": v(23.83, 46.48) * mm, "end": v(1.7, 46.48) * mm});
            skArc(sketch, "E142.1", {"start": v(42.93, 27.38) * mm, "mid": v(37.33, 40.88) * mm, "end": v(23.83, 46.48) * mm});
            skLineSegment(sketch, "E142.2", {"start": v(1.7, 46.48) * mm, "end": v(1.7, 41.24) * mm});
            skLineSegment(sketch, "E142.3", {"start": v(42.93, 27.38) * mm, "end": v(42.93, 20.21) * mm});
            skArc(sketch, "E142.4", {"start": v(23.83, 1.11) * mm, "mid": v(37.33, 6.7) * mm, "end": v(42.93, 20.21) * mm});
            skLineSegment(sketch, "E142.5", {"start": v(1.36, 1.11) * mm, "end": v(23.83, 1.11) * mm});
            skLineSegment(sketch, "E142.6", {"start": v(1.7, 41.24) * mm, "end": v(6.73, 41.24) * mm});
            skLineSegment(sketch, "E142.7", {"start": v(6.73, 41.24) * mm, "end": v(6.73, 6.24) * mm});
            skLineSegment(sketch, "E142.8", {"start": v(6.73, 6.24) * mm, "end": v(1.36, 6.24) * mm});
            skLineSegment(sketch, "E142.9", {"start": v(1.36, 6.24) * mm, "end": v(1.36, 1.11) * mm});
            skArc(sketch, "E143.0", {"start": v(40.93, 27.38) * mm, "mid": v(35.92, 39.47) * mm, "end": v(23.83, 44.48) * mm});
            skLineSegment(sketch, "E143.1", {"start": v(8.73, 40.24) * mm, "end": v(8.73, 7.24) * mm});
            skArc(sketch, "E143.2", {"start": v(8.73, 40.24) * mm, "mid": v(7.85, 42.36) * mm, "end": v(5.73, 43.24) * mm});
            skLineSegment(sketch, "E143.3", {"start": v(3.7, 43.24) * mm, "end": v(5.73, 43.24) * mm});
            skLineSegment(sketch, "E143.4", {"start": v(3.7, 44.48) * mm, "end": v(3.7, 43.24) * mm});
            skArc(sketch, "E143.5", {"start": v(5.73, 4.24) * mm, "mid": v(7.85, 5.12) * mm, "end": v(8.73, 7.24) * mm});
            skLineSegment(sketch, "E143.6", {"start": v(23.83, 44.48) * mm, "end": v(3.7, 44.48) * mm});
            skLineSegment(sketch, "E143.7", {"start": v(5.73, 4.24) * mm, "end": v(3.36, 4.24) * mm});
            skLineSegment(sketch, "E143.8", {"start": v(3.36, 4.24) * mm, "end": v(3.36, 3.11) * mm});
            skLineSegment(sketch, "E143.9", {"start": v(3.36, 3.11) * mm, "end": v(23.83, 3.11) * mm});
            skArc(sketch, "E143.10", {"start": v(23.83, 3.11) * mm, "mid": v(35.92, 8.12) * mm, "end": v(40.93, 20.21) * mm});
            skLineSegment(sketch, "E143.11", {"start": v(40.93, 27.38) * mm, "end": v(40.93, 20.21) * mm});
            skSolve(sketch);
        }
        {
            var Q0;
            Q0 = qSketchRegion(id + "F17", true);
            var Q1;
            Q1=makeQuery(id+"F17.imprint","IMPRINT",FACE,{"disambiguationData":[TD([[makeQuery(id+"F17.imprint","IMPRINT",EDGE,{"derivedFrom":sQuery(id+"F17.wireOp",EDGE,"E139.30")}),1.0]])]});
            var Q2;
            Q2=makeQuery(id+"F17.imprint","IMPRINT",FACE,{"disambiguationData":[TD([[makeQuery(id+"F17.imprint","IMPRINT",EDGE,{"derivedFrom":sQuery(id+"F17.wireOp",EDGE,"E139.25")}),1.0]])]});
            extrude(context, id + "F18", {"entities" : qUnion([Q0, Q1, Q2]), "depth" : 25 * mm});
        }
        {
            var Q0;
            Q0=qCreatedBy(makeId("Front.planeOp"),FACE);
            var sketch = newSketch(context, id + "F19", { "sketchPlane" : qUnion([Q0])});
            skArc(sketch, "E144.0", {"start": v(65.5, 27.94) * mm, "mid": v(62.63, 24.52) * mm, "end": v(60.96, 20.37) * mm});
            skArc(sketch, "E144.1", {"start": v(60.96, 20.37) * mm, "mid": v(60.34, 16.75) * mm, "end": v(60.03, 13.08) * mm});
            skArc(sketch, "E144.2", {"start": v(60.03, 13.08) * mm, "mid": v(59.8, 10.03) * mm, "end": v(59.89, 6.98) * mm});
            skArc(sketch, "E144.3", {"start": v(65.86, 22.25) * mm, "mid": v(67.65, 20.85) * mm, "end": v(69.92, 20.7) * mm});
            skArc(sketch, "E144.4", {"start": v(66.1, 27.52) * mm, "mid": v(65.06, 24.93) * mm, "end": v(65.86, 22.25) * mm});
            skArc(sketch, "E144.5", {"start": v(59.89, 6.98) * mm, "mid": v(60.62, 5.92) * mm, "end": v(61.83, 5.47) * mm});
            skLineSegment(sketch, "E144.6", {"start": v(48.1, 30.42) * mm, "end": v(48.1, 27.61) * mm});
            skLineSegment(sketch, "E144.7", {"start": v(48.1, 30.42) * mm, "end": v(59.09, 30.93) * mm});
            skLineSegment(sketch, "E144.8", {"start": v(48.1, 2.66) * mm, "end": v(64.8, 2.66) * mm});
            skLineSegment(sketch, "E144.9", {"start": v(59.09, 30.93) * mm, "end": v(59.09, 22.2) * mm});
            skLineSegment(sketch, "E144.10", {"start": v(48.1, 5.47) * mm, "end": v(51.51, 5.47) * mm});
            skLineSegment(sketch, "E144.11", {"start": v(48.1, 27.61) * mm, "end": v(51.46, 27.04) * mm});
            skLineSegment(sketch, "E144.12", {"start": v(64.8, 5.47) * mm, "end": v(64.8, 2.66) * mm});
            skLineSegment(sketch, "E144.13", {"start": v(52.29, 26.06) * mm, "end": v(52.51, 6.48) * mm});
            skLineSegment(sketch, "E144.14", {"start": v(61.83, 5.47) * mm, "end": v(64.8, 5.47) * mm});
            skLineSegment(sketch, "E144.15", {"start": v(48.1, 5.47) * mm, "end": v(48.1, 2.66) * mm});
            skArc(sketch, "E144.16", {"start": v(73.07, 24.94) * mm, "mid": v(70.3, 30.62) * mm, "end": v(64, 30.34) * mm});
            skArc(sketch, "E144.17", {"start": v(69.92, 20.7) * mm, "mid": v(72.14, 22.34) * mm, "end": v(73.07, 24.94) * mm});
            skArc(sketch, "E144.18", {"start": v(64, 30.34) * mm, "mid": v(60.9, 26.65) * mm, "end": v(59.09, 22.2) * mm});
            skArc(sketch, "E144.19", {"start": v(51.51, 5.47) * mm, "mid": v(52.22, 5.77) * mm, "end": v(52.51, 6.48) * mm});
            skArc(sketch, "E144.20", {"start": v(66.1, 27.52) * mm, "mid": v(65.98, 27.98) * mm, "end": v(65.5, 27.94) * mm});
            skArc(sketch, "E144.21", {"start": v(52.29, 26.06) * mm, "mid": v(52.05, 26.7) * mm, "end": v(51.46, 27.04) * mm});
            skArc(sketch, "E145.0", {"start": v(63.63, 22.11) * mm, "mid": v(63.9, 21.59) * mm, "end": v(64.23, 21.09) * mm});
            skArc(sketch, "E145.1", {"start": v(63.63, 22.11) * mm, "mid": v(63.22, 21.04) * mm, "end": v(62.91, 19.94) * mm});
            skArc(sketch, "E145.2", {"start": v(62.91, 19.94) * mm, "mid": v(62.32, 16.45) * mm, "end": v(62.03, 12.92) * mm});
            skArc(sketch, "E145.3", {"start": v(62.03, 12.92) * mm, "mid": v(61.81, 10.21) * mm, "end": v(61.86, 7.5) * mm});
            skArc(sketch, "E145.4", {"start": v(61.86, 7.5) * mm, "mid": v(61.89, 7.48) * mm, "end": v(61.92, 7.47) * mm});
            skArc(sketch, "E145.5", {"start": v(64.23, 21.09) * mm, "mid": v(67, 18.96) * mm, "end": v(70.48, 18.78) * mm});
            skLineSegment(sketch, "E145.6", {"start": v(61.92, 7.47) * mm, "end": v(66.8, 7.47) * mm});
            skLineSegment(sketch, "E145.7", {"start": v(66.8, 7.47) * mm, "end": v(66.8, 0.66) * mm});
            skLineSegment(sketch, "E145.8", {"start": v(46.1, 0.66) * mm, "end": v(66.8, 0.66) * mm});
            skLineSegment(sketch, "E145.9", {"start": v(61.09, 33.03) * mm, "end": v(61.09, 30.26) * mm});
            skArc(sketch, "E145.10", {"start": v(62.74, 31.9) * mm, "mid": v(61.89, 31.1) * mm, "end": v(61.09, 30.26) * mm});
            skArc(sketch, "E145.11", {"start": v(75.06, 24.77) * mm, "mid": v(71.24, 32.39) * mm, "end": v(62.74, 31.9) * mm});
            skArc(sketch, "E145.12", {"start": v(70.48, 18.78) * mm, "mid": v(73.7, 21.07) * mm, "end": v(75.06, 24.77) * mm});
            skLineSegment(sketch, "E145.13", {"start": v(46.1, 32.33) * mm, "end": v(61.09, 33.03) * mm});
            skLineSegment(sketch, "E145.14", {"start": v(46.1, 32.33) * mm, "end": v(46.1, 25.92) * mm});
            skLineSegment(sketch, "E145.15", {"start": v(46.1, 25.92) * mm, "end": v(50.3, 25.2) * mm});
            skLineSegment(sketch, "E145.16", {"start": v(50.3, 25.2) * mm, "end": v(50.5, 7.47) * mm});
            skLineSegment(sketch, "E145.17", {"start": v(46.1, 7.47) * mm, "end": v(50.5, 7.47) * mm});
            skLineSegment(sketch, "E145.18", {"start": v(46.1, 7.47) * mm, "end": v(46.1, 0.66) * mm});
            skSolve(sketch);
        }
        {
            var Q0;
            Q0 = qSketchRegion(id + "F19", true);
            extrude(context, id + "F20", {"entities" : qUnion([Q0]), "depth" : 25 * mm});
        }
        {
            var Q0;
            Q0=qCreatedBy(makeId("Front.planeOp"),FACE);
            var sketch = newSketch(context, id + "F21", { "sketchPlane" : qUnion([Q0])});
            skCircle(sketch, "E146.0", {"center": v(80.2, 7.44) * mm, "radius": 5.38 * mm});
            skCircle(sketch, "E147.0", {"center": v(80.2, 7.44) * mm, "radius": 7.38 * mm});
            skSolve(sketch);
        }
        {
            var Q0;
            Q0 = qSketchRegion(id + "F21", true);
            extrude(context, id + "F22", {"entities" : qUnion([Q0]), "depth" : 25 * mm});
        }
    });
